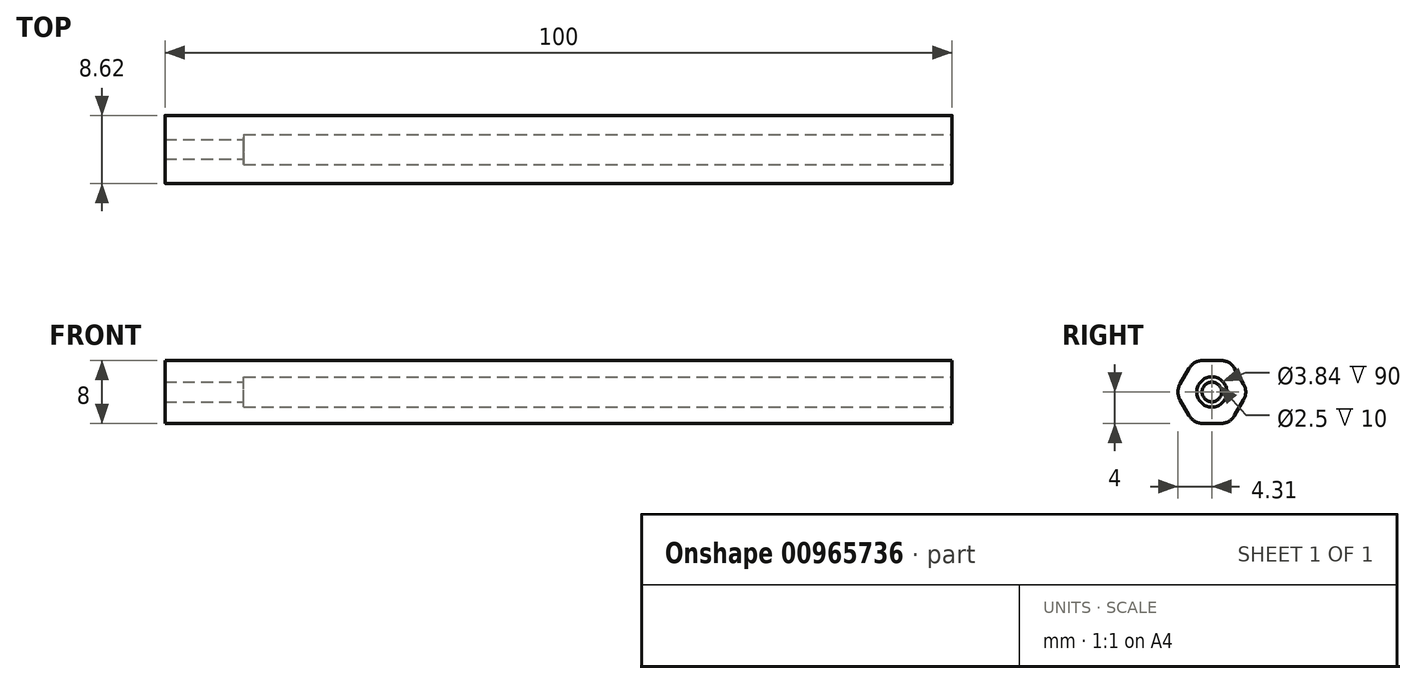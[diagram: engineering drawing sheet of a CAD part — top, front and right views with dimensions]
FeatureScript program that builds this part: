
annotation { "Feature Type Name" : "Feature", "Feature Type Description" : "" }
export const myFeature = defineFeature(function(context is Context, id is Id, definition is map)
    precondition{}
    {
        {
            var Q0;
            Q0=qCreatedBy(makeId("Right.planeOp"),FACE);
            var sketch = newSketch(context, id + "F0", { "sketchPlane" : qUnion([Q0])});
            skCircle(sketch, "E0.cCircle", {"center": v(0, 0) * mm, "radius": 4 * mm, "construction": true});
            skLineSegment(sketch, "E0.0", {"start": v(-2.3, 4) * mm, "end": v(2.3, 4) * mm});
            skLineSegment(sketch, "E0.1", {"start": v(2.3, 4) * mm, "end": v(4.62, 0) * mm});
            skLineSegment(sketch, "E0.2", {"start": v(4.62, 0) * mm, "end": v(2.3, -4) * mm});
            skLineSegment(sketch, "E0.3", {"start": v(2.3, -4) * mm, "end": v(-2.3, -4) * mm});
            skLineSegment(sketch, "E0.4", {"start": v(-2.3, -4) * mm, "end": v(-4.62, 0) * mm});
            skLineSegment(sketch, "E0.5", {"start": v(-4.62, 0) * mm, "end": v(-2.3, 4) * mm});
            skPoint(sketch, "E0.0.midPoint", {"position": v(0, 4) * mm});
            skSolve(sketch);
        }
        {
            var Q0;
            Q0 = qSketchRegion(id + "F0", true);
            var Q1;
            Q1 = qSketchRegion(id + "F3", true);
            extrude(context, id + "F1", {"entities" : qUnion([Q0, Q1]), "depth" : 100 * mm, "offsetDistance" : 25 * mm});
        }
        {
            var Q0;
            Q0=makeQuery(id+"F1.opExtrude","SWEPT_EDGE",EDGE,{"disambiguationData":[OSD([sQuery(id+"F0.wireOp",EDGE,"E0.0"),sQuery(id+"F0.wireOp",EDGE,"E0.5")])]});
            var Q1;
            Q1=makeQuery(id+"F1.opExtrude","SWEPT_EDGE",EDGE,{"disambiguationData":[OSD([sQuery(id+"F0.wireOp",EDGE,"E0.4"),sQuery(id+"F0.wireOp",EDGE,"E0.5")])]});
            var Q2;
            Q2=makeQuery(id+"F1.opExtrude","SWEPT_EDGE",EDGE,{"disambiguationData":[OSD([sQuery(id+"F0.wireOp",EDGE,"E0.3"),sQuery(id+"F0.wireOp",EDGE,"E0.4")])]});
            var Q3;
            Q3=makeQuery(id+"F1.opExtrude","SWEPT_EDGE",EDGE,{"disambiguationData":[OSD([sQuery(id+"F0.wireOp",EDGE,"E0.0"),sQuery(id+"F0.wireOp",EDGE,"E0.1")])]});
            var Q4;
            Q4=makeQuery(id+"F1.opExtrude","SWEPT_EDGE",EDGE,{"disambiguationData":[OSD([sQuery(id+"F0.wireOp",EDGE,"E0.1"),sQuery(id+"F0.wireOp",EDGE,"E0.2")])]});
            var Q5;
            Q5=makeQuery(id+"F1.opExtrude","SWEPT_EDGE",EDGE,{"disambiguationData":[OSD([sQuery(id+"F0.wireOp",EDGE,"E0.2"),sQuery(id+"F0.wireOp",EDGE,"E0.3")])]});
            fillet(context, id + "F2", {"entities" : qUnion([Q0, Q1, Q2, Q3, Q4, Q5]), "radius" : 2 * mm, "tangentPropagation" : true, "allowEdgeOverflow" : false});
        }
        {
            var Q0;
            Q0=makeQuery(id+"F1.opExtrude","CAP_FACE",FACE,{"disambiguationData":[OSD([sQuery(id+"F0.wireOp",EDGE,"E0.0"),sQuery(id+"F0.wireOp",EDGE,"E0.1"),sQuery(id+"F0.wireOp",EDGE,"E0.2"),sQuery(id+"F0.wireOp",EDGE,"E0.3"),sQuery(id+"F0.wireOp",EDGE,"E0.4"),sQuery(id+"F0.wireOp",EDGE,"E0.5")])],"isStart":false});
            var sketch = newSketch(context, id + "F3", { "sketchPlane" : qUnion([Q0])});
            skCircle(sketch, "E1", {"center": v(0, 0) * mm, "radius": 1.92 * mm});
            skSolve(sketch);
        }
        {
            var Q0;
            Q0 = qSketchRegion(id + "F3", true);
            extrude(context, id + "F4", {"entities" : qUnion([Q0]), "operationType" : NewBodyOperationType.REMOVE, "oppositeDirection" : true, "depth" : 90 * mm, "offsetDistance" : 25 * mm});
        }
        {
            var Q0;
            Q0=makeQuery(id+"F4.boolean.opBoolean","COPY",FACE,{"derivedFrom":makeQuery(id+"F4.opExtrude","CAP_FACE",FACE,{"disambiguationData":[OSD([sQuery(id+"F3.wireOp",EDGE,"E1")])],"isStart":false})});
            var sketch = newSketch(context, id + "F5", { "sketchPlane" : qUnion([Q0])});
            skCircle(sketch, "E2", {"center": v(0, 0) * mm, "radius": 1.25 * mm});
            skSolve(sketch);
        }
        {
            var Q0;
            Q0 = qSketchRegion(id + "F5", true);
            extrude(context, id + "F6", {"entities" : qUnion([Q0]), "operationType" : NewBodyOperationType.REMOVE, "oppositeDirection" : true, "depth" : 20 * mm, "offsetDistance" : 25 * mm});
        }
    });
